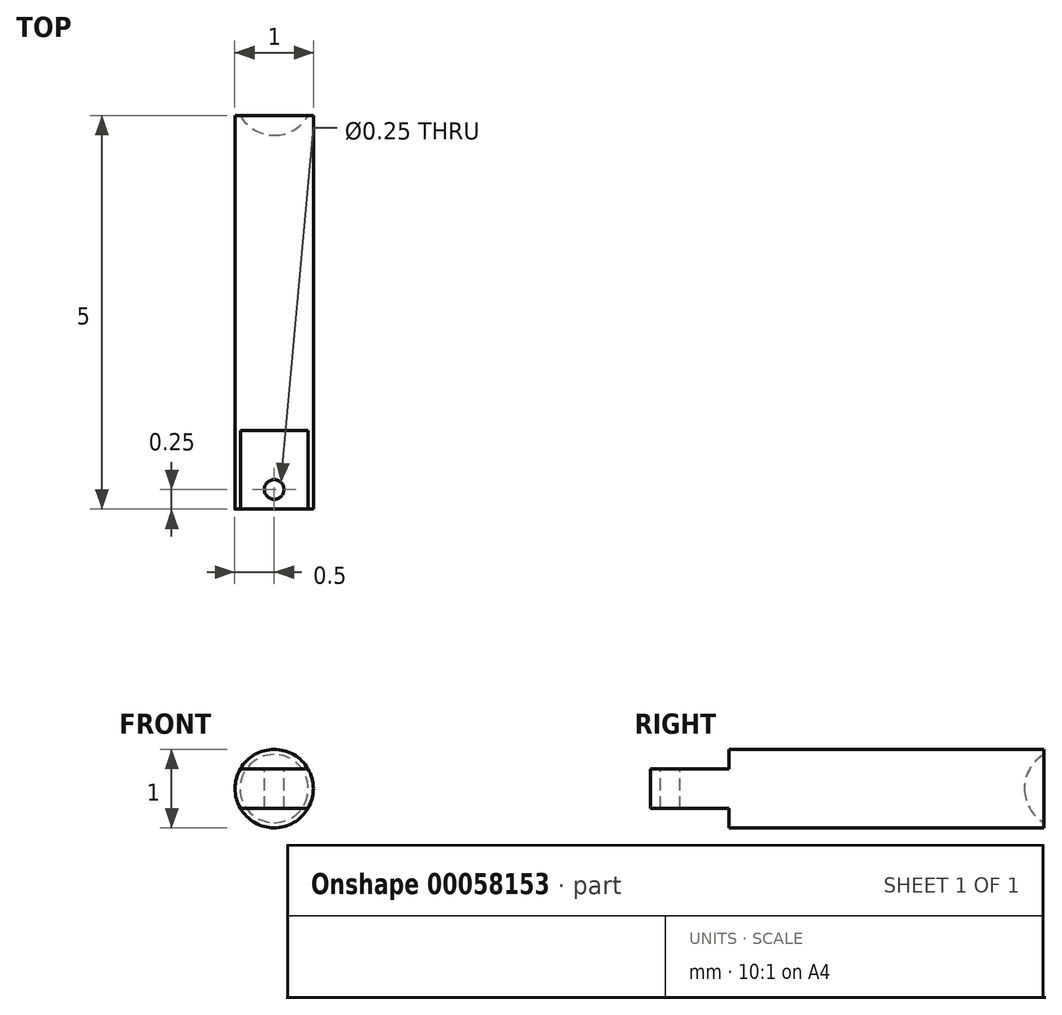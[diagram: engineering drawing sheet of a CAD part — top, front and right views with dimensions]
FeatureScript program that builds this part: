
annotation { "Feature Type Name" : "Feature", "Feature Type Description" : "" }
export const myFeature = defineFeature(function(context is Context, id is Id, definition is map)
    precondition{}
    {
        {
            var Q0;
            Q0=qCreatedBy(makeId("Front.planeOp"),FACE);
            var sketch = newSketch(context, id + "F0", { "sketchPlane" : qUnion([Q0])});
            skCircle(sketch, "E0", {"center": v(0, 0) * mm, "radius": 0.5 * mm});
            skSolve(sketch);
        }
        {
            var Q0;
            Q0 = qSketchRegion(id + "F0", true);
            extrude(context, id + "F1", {"entities" : qUnion([Q0]), "endBound" : BoundingType.SYMMETRIC, "depth" : 5 * mm});
        }
        {
            var Q0;
            Q0=qCreatedBy(makeId("Right.planeOp"),FACE);
            var sketch = newSketch(context, id + "F2", { "sketchPlane" : qUnion([Q0])});
            skLineSegment(sketch, "E1.bottom", {"start": v(-2.5, 0.73) * mm, "end": v(-1.5, 0.73) * mm});
            skLineSegment(sketch, "E1.top", {"start": v(-2.5, 0.25) * mm, "end": v(-1.5, 0.25) * mm});
            skLineSegment(sketch, "E1.left", {"start": v(-2.5, 0.73) * mm, "end": v(-2.5, 0.25) * mm});
            skLineSegment(sketch, "E1.right", {"start": v(-1.5, 0.73) * mm, "end": v(-1.5, 0.25) * mm});
            skLineSegment(sketch, "E2.bottom", {"start": v(-2.5, -0.25) * mm, "end": v(-1.5, -0.25) * mm});
            skLineSegment(sketch, "E2.top", {"start": v(-2.5, -0.9) * mm, "end": v(-1.5, -0.9) * mm});
            skLineSegment(sketch, "E2.left", {"start": v(-2.5, -0.25) * mm, "end": v(-2.5, -0.9) * mm});
            skLineSegment(sketch, "E2.right", {"start": v(-1.5, -0.25) * mm, "end": v(-1.5, -0.9) * mm});
            skSolve(sketch);
        }
        {
            var Q0;
            Q0 = qSketchRegion(id + "F2", true);
            extrude(context, id + "F3", {"entities" : qUnion([Q0]), "operationType" : NewBodyOperationType.REMOVE, "endBound" : BoundingType.THROUGH_ALL, "oppositeDirection" : true, "depth" : 25 * mm, "hasSecondDirection" : true, "secondDirectionBound" : SecondDirectionBoundingType.THROUGH_ALL, "secondDirectionOppositeDirection" : false, "secondDirectionDepth" : 25 * mm});
        }
        {
            var Q0;
            Q0=qCreatedBy(makeId("Right.planeOp"),FACE);
            var sketch = newSketch(context, id + "F4", { "sketchPlane" : qUnion([Q0])});
            skArc(sketch, "E3", {"start": v(2.5, 0.43) * mm, "mid": v(2.32, 0.25) * mm, "end": v(2.25, 0) * mm});
            skLineSegment(sketch, "E4", {"start": v(2.5, 0.43) * mm, "end": v(2.5, 0) * mm});
            skLineSegment(sketch, "E5", {"start": v(2.5, 0) * mm, "end": v(2.25, 0) * mm});
            skSolve(sketch);
        }
        {
            var Q0;
            Q0 = qSketchRegion(id + "F4", true);
            var Q1;
            Q1=sQuery(id+"F4.wireOp",EDGE,"E5");
            revolve(context, id + "F5", {"operationType" : NewBodyOperationType.REMOVE, "entities" : qUnion([Q0]), "axis" : qUnion([Q1]), "revolveType" : RevolveType.FULL, "oppositeDirection" : true});
        }
        {
            var Q0;
            Q0=makeQuery(id+"F3.boolean.opBoolean","COPY",FACE,{"derivedFrom":makeQuery(id+"F3.opExtrude","SWEPT_FACE",FACE,{"disambiguationData":[OSD([sQuery(id+"F2.wireOp",EDGE,"E1.top")])]})});
            var sketch = newSketch(context, id + "F6", { "sketchPlane" : qUnion([Q0])});
            skCircle(sketch, "E6", {"center": v(0, -2.25) * mm, "radius": 0.12 * mm});
            skSolve(sketch);
        }
        {
            var Q0;
            Q0 = qSketchRegion(id + "F6", true);
            extrude(context, id + "F7", {"entities" : qUnion([Q0]), "operationType" : NewBodyOperationType.REMOVE, "oppositeDirection" : true, "depth" : 25 * mm});
        }
    });
